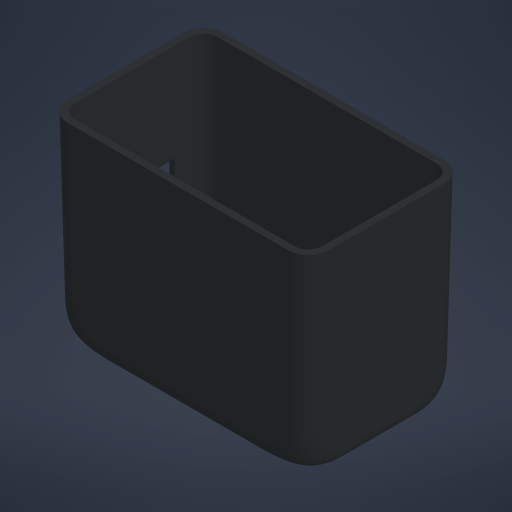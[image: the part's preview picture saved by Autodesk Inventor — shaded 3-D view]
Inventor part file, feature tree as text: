
AUTODESK INVENTOR PART (.ipt)
format: ipt  version: 2024 (Build 280153000, 153)  size: 467,968 bytes
history: native  units: in
note: dims shown in document units (in); Inventor stores cm internally (conversion verified against a paired STEP export)
features: chamfer x9, extrude x3, fillet x3, plane x2, sketch x2, boolean_combine x1, thicken_offset x1
ambient origin geometry x8: Origin, YZ Plane, XZ Plane, XY Plane, X Axis, Y Axis, Z Axis, Center Point
bodies: Solid1 (feature_tree), Solid3 (feature_tree)
feature tree (21):
  extrude  "Extrusion1"  Depth=1.761in
  chamfer  "Chamfer1"  Distance=1.301in
  chamfer  "Chamfer3"  Distance=1.665in
  chamfer  "Chamfer4"  Distance=1.665in
  chamfer  "Chamfer5"  Distance=1.665in
  chamfer  "Chamfer6"  Distance=1.665in
  fillet  "Fillet2"  Radius=0.53in
  plane  "Work Plane8"
  extrude  "Extrusion8"  Depth=0.0104in
  boolean_combine  "Combine3"
  thicken_offset  "Thicken9"
  chamfer  "Chamfer12"  Distance=0.0625in
  chamfer  "Chamfer13"  Distance=0.0625in
  chamfer  "Chamfer14"  Distance=0.0625in
  chamfer  "Chamfer15"  Distance=0.0625in
  fillet  "Fillet8"  Radius=0.0625in
  plane  "Work Plane16"
  extrude  "Extrusion12"  Depth=0.0104in TaperAngle=0.0deg
  fillet  "Fillet9"  Radius=0.0625in
  sketch  "Sketch11"  dims[d0=2.257in d1=1.761in d2=1.301in d3=0.0in]
  sketch  "Sketch20"  dims[d12=0.52in d30=0.1in d31=0.125in d32=0.2749in d36=1.665in d37=0.125in d38=0.0069in d39=1.665in d40=0.125in d41=0.0069in d42=1.665in d43=0.125in d44=0.0069in d45=1.665in d46=0.125in d47=0.0069in d48=0.53in d49=0.53in d78=1.0in d89=0.0625in d90=0.0625in d91=0.0625in d92=0.0625in d93=0.0625in d94=1.8045in d95=0.0in d134=0.0625in d135=0.125in d160=0.0008in d161=0.0008in d163=1.8in d164=0.125in d165=0.0069in d166=1.8in d167=0.125in d168=0.0069in d169=1.8in d170=0.125in d171=0.0069in d172=1.8in d173=0.125in d174=0.0069in d176=0.15in d177=0.1885in d178=0.5in d179=0.375in d180=0.375in d181=0.375in d182=0.5in d183=0.375in d184=0.5in d185=0.375in d186=0.375in d187=0.375in d188=0.5in d189=0.375in d190=0.1875in d191=0.45in d192=0.135in d193=0.41in d194=0.509in d195=1.301in d196=0.0in d197=0.0156in d198=0.0104in d136=0.0in d137=0.0in]
